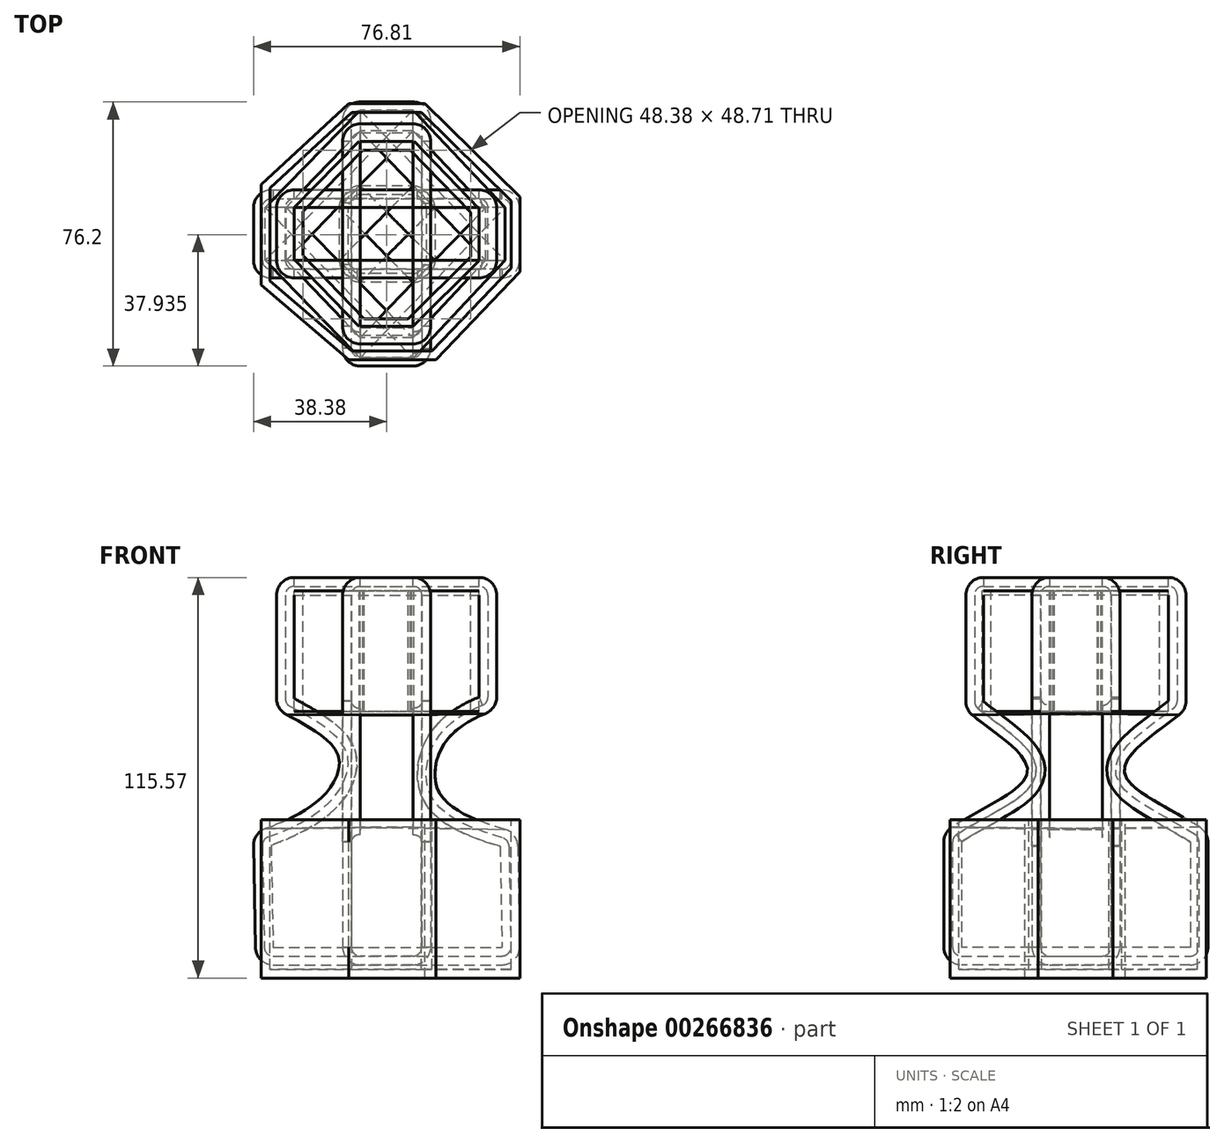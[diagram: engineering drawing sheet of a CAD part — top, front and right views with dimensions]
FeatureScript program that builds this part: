
annotation { "Feature Type Name" : "Feature", "Feature Type Description" : "" }
export const myFeature = defineFeature(function(context is Context, id is Id, definition is map)
    precondition{}
    {
        {
            var Q0;
            Q0=qCreatedBy(makeId("Front.planeOp"),FACE);
            var sketch = newSketch(context, id + "F0", { "sketchPlane" : qUnion([Q0])});
            skLineSegment(sketch, "E0.bottom", {"start": v(-38.45, 19.05) * mm, "end": v(37.75, 19.05) * mm});
            skLineSegment(sketch, "E0.top", {"start": v(-37.75, -19.05) * mm, "end": v(38.45, -19.05) * mm});
            skLineSegment(sketch, "E0.left", {"start": v(-38.45, 19.05) * mm, "end": v(-37.75, -19.05) * mm});
            skLineSegment(sketch, "E0.right", {"start": v(37.75, 19.05) * mm, "end": v(38.45, -19.05) * mm});
            skPoint(sketch, "E0.middle", {"position": v(0, 0) * mm});
            skLineSegment(sketch, "E1.bottom", {"start": v(-31.75, 92.7) * mm, "end": v(31.75, 92.7) * mm});
            skLineSegment(sketch, "E1.top", {"start": v(-31.75, 54.6) * mm, "end": v(31.75, 54.6) * mm});
            skLineSegment(sketch, "E1.left", {"start": v(-31.75, 92.7) * mm, "end": v(-31.75, 54.6) * mm});
            skLineSegment(sketch, "E1.right", {"start": v(31.75, 92.7) * mm, "end": v(31.75, 54.6) * mm});
            skPoint(sketch, "E1.middle", {"position": v(0, 73.66) * mm});
            skFitSpline(sketch, "E2", {"points": [v(31.75, 54.6) * mm, v(13.97, 36.83) * mm, v(37.75, 19.05) * mm], "startDerivative": vector(-85.25, -26.82) * mm, "endDerivative": vector(119.34, -30.7) * mm});
            skFitSpline(sketch, "E3", {"points": [v(-31.75, 54.6) * mm, v(-13.97, 36.83) * mm, v(-38.45, 19.05) * mm], "startDerivative": vector(109.16, -53.78) * mm, "endDerivative": vector(-101.51, -32.91) * mm});
            skSolve(sketch);
        }
        {
            var Q0;
            Q0=makeQuery(id+"F0.imprint","IMPRINT",FACE,{"disambiguationData":[TD([[makeQuery(id+"F0.imprint","IMPRINT",EDGE,{"derivedFrom":sQuery(id+"F0.wireOp",EDGE,"E1.bottom")}),-1.0]])]});
            var Q1;
            Q1=makeQuery(id+"F0.imprint","IMPRINT",FACE,{"disambiguationData":[TD([[makeQuery(id+"F0.imprint","IMPRINT",EDGE,{"derivedFrom":sQuery(id+"F0.wireOp",EDGE,"E0.bottom")}),-1.0]])]});
            var Q2;
            Q2=makeQuery(id+"F0.imprint","IMPRINT",FACE,{"disambiguationData":[TD([[makeQuery(id+"F0.imprint","IMPRINT",EDGE,{"derivedFrom":sQuery(id+"F0.wireOp",EDGE,"E0.bottom")}),1.0]])]});
            extrude(context, id + "F1", {"entities" : qUnion([Q0, Q1, Q2]), "endBound" : BoundingType.SYMMETRIC, "depth" : 25.4 * mm});
        }
        {
            var Q0;
            Q0=qCreatedBy(makeId("Right.planeOp"),FACE);
            var sketch = newSketch(context, id + "F2", { "sketchPlane" : qUnion([Q0])});
            skLineSegment(sketch, "E4.bottom", {"start": v(38.1, 19.05) * mm, "end": v(-38.1, 19.05) * mm});
            skLineSegment(sketch, "E4.top", {"start": v(38.1, -19.05) * mm, "end": v(-38.1, -19.05) * mm});
            skLineSegment(sketch, "E4.left", {"start": v(38.1, 19.05) * mm, "end": v(38.1, -19.05) * mm});
            skLineSegment(sketch, "E4.right", {"start": v(-38.1, 19.05) * mm, "end": v(-38.1, -19.05) * mm});
            skPoint(sketch, "E4.middle", {"position": v(0, 0) * mm});
            skLineSegment(sketch, "E5.bottom", {"start": v(31.75, 54.61) * mm, "end": v(-31.75, 54.6) * mm});
            skLineSegment(sketch, "E5.top", {"start": v(31.75, 92.7) * mm, "end": v(-31.75, 92.7) * mm});
            skLineSegment(sketch, "E5.left", {"start": v(31.75, 54.61) * mm, "end": v(31.75, 92.7) * mm});
            skLineSegment(sketch, "E5.right", {"start": v(-31.75, 54.6) * mm, "end": v(-31.75, 92.7) * mm});
            skPoint(sketch, "E5.middle", {"position": v(0, 73.66) * mm});
            skFitSpline(sketch, "E6", {"points": [v(31.75, 54.61) * mm, v(13.97, 36.83) * mm, v(38.1, 19.05) * mm], "startDerivative": vector(-45.66, -37.2) * mm, "endDerivative": vector(56.1, -40.08) * mm});
            skFitSpline(sketch, "E7", {"points": [v(-31.75, 54.6) * mm, v(-13.97, 36.83) * mm, v(-38.1, 19.05) * mm], "startDerivative": vector(37.02, -34.46) * mm, "endDerivative": vector(-47.7, -36.6) * mm});
            skSolve(sketch);
        }
        {
            var Q0;
            Q0=makeQuery(id+"F2.imprint","IMPRINT",FACE,{"disambiguationData":[TD([[makeQuery(id+"F2.imprint","IMPRINT",EDGE,{"derivedFrom":sQuery(id+"F2.wireOp",EDGE,"E5.bottom")}),-1.0]])]});
            var Q1;
            Q1=makeQuery(id+"F2.imprint","IMPRINT",FACE,{"disambiguationData":[TD([[makeQuery(id+"F2.imprint","IMPRINT",EDGE,{"derivedFrom":sQuery(id+"F2.wireOp",EDGE,"E4.bottom")}),-1.0]])]});
            var Q2;
            Q2=makeQuery(id+"F2.imprint","IMPRINT",FACE,{"disambiguationData":[TD([[makeQuery(id+"F2.imprint","IMPRINT",EDGE,{"derivedFrom":sQuery(id+"F2.wireOp",EDGE,"E4.bottom")}),1.0]])]});
            extrude(context, id + "F3", {"entities" : qUnion([Q0, Q1, Q2]), "endBound" : BoundingType.SYMMETRIC, "depth" : 25.4 * mm});
        }
        {
            var Q0;
            Q0=makeQuery(id+"F1.opExtrude","SWEPT_EDGE",EDGE,{"disambiguationData":[OSD([sQuery(id+"F0.wireOp",EDGE,"E1.bottom"),sQuery(id+"F0.wireOp",EDGE,"E1.right")])]});
            var Q1;
            Q1=makeQuery(id+"F1.opExtrude","SWEPT_EDGE",EDGE,{"disambiguationData":[OSD([sQuery(id+"F0.wireOp",EDGE,"E0.top"),sQuery(id+"F0.wireOp",EDGE,"E0.right")])]});
            var Q2;
            Q2=makeQuery(id+"F1.opExtrude","SWEPT_EDGE",EDGE,{"disambiguationData":[OSD([sQuery(id+"F0.wireOp",EDGE,"E0.top"),sQuery(id+"F0.wireOp",EDGE,"E0.left")])]});
            var Q3;
            Q3=makeQuery(id+"F1.opExtrude","CAP_EDGE",EDGE,{"disambiguationData":[OSD([sQuery(id+"F0.wireOp",EDGE,"E0.right")])],"isStart":false});
            var Q4;
            Q4=makeQuery(id+"F1.opExtrude","CAP_EDGE",EDGE,{"disambiguationData":[OSD([sQuery(id+"F0.wireOp",EDGE,"E2")])],"isStart":false});
            var Q5;
            Q5=makeQuery(id+"F1.opExtrude","CAP_EDGE",EDGE,{"disambiguationData":[OSD([sQuery(id+"F0.wireOp",EDGE,"E2")])],"isStart":true});
            var Q6;
            Q6=makeQuery(id+"F3.opExtrude","CAP_EDGE",EDGE,{"disambiguationData":[OSD([sQuery(id+"F2.wireOp",EDGE,"E7")])],"isStart":false});
            var Q7;
            Q7=makeQuery(id+"F3.opExtrude","CAP_EDGE",EDGE,{"disambiguationData":[OSD([sQuery(id+"F2.wireOp",EDGE,"E5.right")])],"isStart":false});
            var Q8;
            Q8=makeQuery(id+"F3.opExtrude","CAP_EDGE",EDGE,{"disambiguationData":[OSD([sQuery(id+"F2.wireOp",EDGE,"E6")])],"isStart":false});
            var Q9;
            Q9=makeQuery(id+"F3.opExtrude","CAP_EDGE",EDGE,{"disambiguationData":[OSD([sQuery(id+"F2.wireOp",EDGE,"E5.left")])],"isStart":true});
            var Q10;
            Q10=makeQuery(id+"F3.opExtrude","CAP_EDGE",EDGE,{"disambiguationData":[OSD([sQuery(id+"F2.wireOp",EDGE,"E5.left")])],"isStart":false});
            var Q11;
            Q11=makeQuery(id+"F3.opExtrude","CAP_EDGE",EDGE,{"disambiguationData":[OSD([sQuery(id+"F2.wireOp",EDGE,"E6")])],"isStart":true});
            var Q12;
            Q12=makeQuery(id+"F1.opExtrude","CAP_EDGE",EDGE,{"disambiguationData":[OSD([sQuery(id+"F0.wireOp",EDGE,"E0.right")])],"isStart":true});
            var Q13;
            Q13=makeQuery(id+"F1.opExtrude","CAP_EDGE",EDGE,{"disambiguationData":[OSD([sQuery(id+"F0.wireOp",EDGE,"E0.left")])],"isStart":false});
            var Q14;
            Q14=makeQuery(id+"F1.opExtrude","CAP_EDGE",EDGE,{"disambiguationData":[OSD([sQuery(id+"F0.wireOp",EDGE,"E0.top")])],"isStart":false});
            var Q15;
            Q15=makeQuery(id+"F1.opExtrude","CAP_EDGE",EDGE,{"disambiguationData":[OSD([sQuery(id+"F0.wireOp",EDGE,"E0.top")])],"isStart":true});
            var Q16;
            Q16=makeQuery(id+"F1.opExtrude","SWEPT_EDGE",EDGE,{"disambiguationData":[OSD([sQuery(id+"F0.wireOp",EDGE,"E1.top"),sQuery(id+"F0.wireOp",EDGE,"E1.right"),sQuery(id+"F0.wireOp",EDGE,"E2")])]});
            var Q17;
            Q17=makeQuery(id+"F1.opExtrude","SWEPT_EDGE",EDGE,{"disambiguationData":[OSD([sQuery(id+"F0.wireOp",EDGE,"E1.bottom"),sQuery(id+"F0.wireOp",EDGE,"E1.left")])]});
            var Q18;
            Q18=makeQuery(id+"F1.opExtrude","SWEPT_EDGE",EDGE,{"disambiguationData":[OSD([sQuery(id+"F0.wireOp",EDGE,"E0.bottom"),sQuery(id+"F0.wireOp",EDGE,"E0.right"),sQuery(id+"F0.wireOp",EDGE,"E2")])]});
            var Q19;
            Q19=makeQuery(id+"F1.opExtrude","CAP_EDGE",EDGE,{"disambiguationData":[OSD([sQuery(id+"F0.wireOp",EDGE,"E1.bottom")])],"isStart":false});
            var Q20;
            Q20=makeQuery(id+"F1.opExtrude","CAP_EDGE",EDGE,{"disambiguationData":[OSD([sQuery(id+"F0.wireOp",EDGE,"E1.bottom")])],"isStart":true});
            var Q21;
            Q21=makeQuery(id+"F1.opExtrude","CAP_EDGE",EDGE,{"disambiguationData":[OSD([sQuery(id+"F0.wireOp",EDGE,"E3")])],"isStart":false});
            var Q22;
            Q22=makeQuery(id+"F1.opExtrude","CAP_EDGE",EDGE,{"disambiguationData":[OSD([sQuery(id+"F0.wireOp",EDGE,"E3")])],"isStart":true});
            var Q23;
            Q23=makeQuery(id+"F1.opExtrude","CAP_EDGE",EDGE,{"disambiguationData":[OSD([sQuery(id+"F0.wireOp",EDGE,"E1.right")])],"isStart":false});
            var Q24;
            Q24=makeQuery(id+"F1.opExtrude","CAP_EDGE",EDGE,{"disambiguationData":[OSD([sQuery(id+"F0.wireOp",EDGE,"E1.right")])],"isStart":true});
            var Q25;
            Q25=makeQuery(id+"F3.opExtrude","CAP_EDGE",EDGE,{"disambiguationData":[OSD([sQuery(id+"F2.wireOp",EDGE,"E4.left")])],"isStart":true});
            var Q26;
            Q26=makeQuery(id+"F3.opExtrude","CAP_EDGE",EDGE,{"disambiguationData":[OSD([sQuery(id+"F2.wireOp",EDGE,"E4.left")])],"isStart":false});
            var Q27;
            Q27=makeQuery(id+"F3.opExtrude","CAP_EDGE",EDGE,{"disambiguationData":[OSD([sQuery(id+"F2.wireOp",EDGE,"E7")])],"isStart":true});
            var Q28;
            Q28=makeQuery(id+"F3.opExtrude","CAP_EDGE",EDGE,{"disambiguationData":[OSD([sQuery(id+"F2.wireOp",EDGE,"E5.top")])],"isStart":false});
            var Q29;
            Q29=makeQuery(id+"F3.opExtrude","SWEPT_EDGE",EDGE,{"disambiguationData":[OSD([sQuery(id+"F2.wireOp",EDGE,"E4.top"),sQuery(id+"F2.wireOp",EDGE,"E4.left")])]});
            var Q30;
            Q30=makeQuery(id+"F3.opExtrude","CAP_EDGE",EDGE,{"disambiguationData":[OSD([sQuery(id+"F2.wireOp",EDGE,"E4.right")])],"isStart":false});
            var Q31;
            Q31=makeQuery(id+"F3.opExtrude","SWEPT_EDGE",EDGE,{"disambiguationData":[OSD([sQuery(id+"F2.wireOp",EDGE,"E5.bottom"),sQuery(id+"F2.wireOp",EDGE,"E5.left"),sQuery(id+"F2.wireOp",EDGE,"E6")])]});
            var Q32;
            Q32=makeQuery(id+"F3.opExtrude","CAP_EDGE",EDGE,{"disambiguationData":[OSD([sQuery(id+"F2.wireOp",EDGE,"E4.top")])],"isStart":true});
            var Q33;
            Q33=makeQuery(id+"F3.opExtrude","CAP_EDGE",EDGE,{"disambiguationData":[OSD([sQuery(id+"F2.wireOp",EDGE,"E4.right")])],"isStart":true});
            var Q34;
            Q34=makeQuery(id+"F3.opExtrude","SWEPT_EDGE",EDGE,{"disambiguationData":[OSD([sQuery(id+"F2.wireOp",EDGE,"E4.bottom"),sQuery(id+"F2.wireOp",EDGE,"E4.left"),sQuery(id+"F2.wireOp",EDGE,"E6")])]});
            var Q35;
            Q35=makeQuery(id+"F3.opExtrude","CAP_EDGE",EDGE,{"disambiguationData":[OSD([sQuery(id+"F2.wireOp",EDGE,"E4.top")])],"isStart":false});
            var Q36;
            Q36=makeQuery(id+"F3.opExtrude","CAP_EDGE",EDGE,{"disambiguationData":[OSD([sQuery(id+"F2.wireOp",EDGE,"E5.top")])],"isStart":true});
            var Q37;
            Q37=makeQuery(id+"F3.opExtrude","SWEPT_EDGE",EDGE,{"disambiguationData":[OSD([sQuery(id+"F2.wireOp",EDGE,"E5.bottom"),sQuery(id+"F2.wireOp",EDGE,"E5.right"),sQuery(id+"F2.wireOp",EDGE,"E7")])]});
            var Q38;
            Q38=makeQuery(id+"F1.opExtrude","CAP_EDGE",EDGE,{"disambiguationData":[OSD([sQuery(id+"F0.wireOp",EDGE,"E1.left")])],"isStart":false});
            var Q39;
            Q39=makeQuery(id+"F1.opExtrude","CAP_EDGE",EDGE,{"disambiguationData":[OSD([sQuery(id+"F0.wireOp",EDGE,"E1.left")])],"isStart":true});
            var Q40;
            Q40=makeQuery(id+"F1.opExtrude","CAP_EDGE",EDGE,{"disambiguationData":[OSD([sQuery(id+"F0.wireOp",EDGE,"E0.left")])],"isStart":true});
            var Q41;
            Q41=makeQuery(id+"F1.opExtrude","SWEPT_EDGE",EDGE,{"disambiguationData":[OSD([sQuery(id+"F0.wireOp",EDGE,"E1.top"),sQuery(id+"F0.wireOp",EDGE,"E1.left"),sQuery(id+"F0.wireOp",EDGE,"E3")])]});
            var Q42;
            Q42=makeQuery(id+"F1.opExtrude","SWEPT_EDGE",EDGE,{"disambiguationData":[OSD([sQuery(id+"F0.wireOp",EDGE,"E0.bottom"),sQuery(id+"F0.wireOp",EDGE,"E0.left"),sQuery(id+"F0.wireOp",EDGE,"E3")])]});
            var Q43;
            Q43=makeQuery(id+"F3.opExtrude","SWEPT_EDGE",EDGE,{"disambiguationData":[OSD([sQuery(id+"F2.wireOp",EDGE,"E4.bottom"),sQuery(id+"F2.wireOp",EDGE,"E4.right"),sQuery(id+"F2.wireOp",EDGE,"E7")])]});
            var Q44;
            Q44=makeQuery(id+"F3.opExtrude","SWEPT_EDGE",EDGE,{"disambiguationData":[OSD([sQuery(id+"F2.wireOp",EDGE,"E5.top"),sQuery(id+"F2.wireOp",EDGE,"E5.right")])]});
            var Q45;
            Q45=makeQuery(id+"F3.opExtrude","SWEPT_EDGE",EDGE,{"disambiguationData":[OSD([sQuery(id+"F2.wireOp",EDGE,"E5.top"),sQuery(id+"F2.wireOp",EDGE,"E5.left")])]});
            var Q46;
            Q46=makeQuery(id+"F3.opExtrude","CAP_EDGE",EDGE,{"disambiguationData":[OSD([sQuery(id+"F2.wireOp",EDGE,"E5.right")])],"isStart":true});
            var Q47;
            Q47=makeQuery(id+"F3.opExtrude","SWEPT_EDGE",EDGE,{"disambiguationData":[OSD([sQuery(id+"F2.wireOp",EDGE,"E4.top"),sQuery(id+"F2.wireOp",EDGE,"E4.right")])]});
            fillet(context, id + "F4", {"entities" : qUnion([Q0, Q1, Q2, Q3, Q4, Q5, Q6, Q7, Q8, Q9, Q10, Q11, Q12, Q13, Q14, Q15, Q16, Q17, Q18, Q19, Q20, Q21, Q22, Q23, Q24, Q25, Q26, Q27, Q28, Q29, Q30, Q31, Q32, Q33, Q34, Q35, Q36, Q37, Q38, Q39, Q40, Q41, Q42, Q43, Q44, Q45, Q46, Q47]), "radius" : 5.08 * mm, "tangentPropagation" : true, "allowEdgeOverflow" : false});
        }
        {
            var Q0;
            Q0=makeQuery(id+"F1.opExtrude","SWEPT_FACE",FACE,{"disambiguationData":[OSD([sQuery(id+"F0.wireOp",EDGE,"E1.bottom")])]});
            var Q1;
            Q1=makeQuery(id+"F3.opExtrude","SWEPT_FACE",FACE,{"disambiguationData":[OSD([sQuery(id+"F2.wireOp",EDGE,"E5.top")])]});
            var Q2;
            Q2=makeQuery(id+"F3.opExtrude","CAP_FACE",FACE,{"disambiguationData":[OSD([sQuery(id+"F2.wireOp",EDGE,"E4.top"),sQuery(id+"F2.wireOp",EDGE,"E4.left"),sQuery(id+"F2.wireOp",EDGE,"E4.right"),sQuery(id+"F2.wireOp",EDGE,"E5.top"),sQuery(id+"F2.wireOp",EDGE,"E5.left"),sQuery(id+"F2.wireOp",EDGE,"E5.right"),sQuery(id+"F2.wireOp",EDGE,"E6"),sQuery(id+"F2.wireOp",EDGE,"E7")])],"isStart":true});
            var Q3;
            Q3=makeQuery(id+"F1.opExtrude","CAP_FACE",FACE,{"disambiguationData":[OSD([sQuery(id+"F0.wireOp",EDGE,"E0.top"),sQuery(id+"F0.wireOp",EDGE,"E0.left"),sQuery(id+"F0.wireOp",EDGE,"E0.right"),sQuery(id+"F0.wireOp",EDGE,"E1.bottom"),sQuery(id+"F0.wireOp",EDGE,"E1.left"),sQuery(id+"F0.wireOp",EDGE,"E1.right"),sQuery(id+"F0.wireOp",EDGE,"E2"),sQuery(id+"F0.wireOp",EDGE,"E3")])],"isStart":true});
            var Q4;
            Q4=makeQuery(id+"F3.opExtrude","CAP_FACE",FACE,{"disambiguationData":[OSD([sQuery(id+"F2.wireOp",EDGE,"E4.top"),sQuery(id+"F2.wireOp",EDGE,"E4.left"),sQuery(id+"F2.wireOp",EDGE,"E4.right"),sQuery(id+"F2.wireOp",EDGE,"E5.top"),sQuery(id+"F2.wireOp",EDGE,"E5.left"),sQuery(id+"F2.wireOp",EDGE,"E5.right"),sQuery(id+"F2.wireOp",EDGE,"E6"),sQuery(id+"F2.wireOp",EDGE,"E7")])],"isStart":false});
            var Q5;
            Q5=makeQuery(id+"F1.opExtrude","CAP_FACE",FACE,{"disambiguationData":[OSD([sQuery(id+"F0.wireOp",EDGE,"E0.top"),sQuery(id+"F0.wireOp",EDGE,"E0.left"),sQuery(id+"F0.wireOp",EDGE,"E0.right"),sQuery(id+"F0.wireOp",EDGE,"E1.bottom"),sQuery(id+"F0.wireOp",EDGE,"E1.left"),sQuery(id+"F0.wireOp",EDGE,"E1.right"),sQuery(id+"F0.wireOp",EDGE,"E2"),sQuery(id+"F0.wireOp",EDGE,"E3")])],"isStart":false});
            shell(context, id + "F5", {"entities" : qUnion([Q0, Q1, Q2, Q3, Q4, Q5]), "thickness" : 2.54 * mm});
        }
        {
            var Q0;
            Q0=qCreatedBy(makeId("Top.planeOp"),FACE);
            var sketch = newSketch(context, id + "F6", { "sketchPlane" : qUnion([Q0])});
            skLineSegment(sketch, "E8", {"start": v(-11.25, 34.28) * mm, "end": v(-10.99, 34.28) * mm});
            skLineSegment(sketch, "E9", {"start": v(-36.23, 14.3) * mm, "end": v(-10.99, 37.64) * mm});
            skLineSegment(sketch, "E10", {"start": v(-10.99, 37.64) * mm, "end": v(11.02, 37.64) * mm});
            skLineSegment(sketch, "E11", {"start": v(11.02, 37.64) * mm, "end": v(38.43, 10.67) * mm});
            skLineSegment(sketch, "E12", {"start": v(38.43, 10.67) * mm, "end": v(38.43, -10.95) * mm});
            skLineSegment(sketch, "E13", {"start": v(38.43, -10.95) * mm, "end": v(14.16, -36.26) * mm});
            skLineSegment(sketch, "E14", {"start": v(14.16, -36.26) * mm, "end": v(-10.95, -36.26) * mm});
            skLineSegment(sketch, "E15", {"start": v(-10.95, -36.26) * mm, "end": v(-36.23, -14.73) * mm});
            skLineSegment(sketch, "E16", {"start": v(-36.23, -14.73) * mm, "end": v(-36.23, 14.3) * mm});
            skSolve(sketch);
        }
        {
            var Q0;
            Q0 = qSketchRegion(id + "F6", true);
            extrude(context, id + "F7", {"entities" : qUnion([Q0]), "endBound" : BoundingType.SYMMETRIC, "oppositeDirection" : true, "depth" : 45.72 * mm});
        }
        {
            var Q0;
            Q0=makeQuery(id+"F7.opExtrude","CAP_FACE",FACE,{"disambiguationData":[OSD([sQuery(id+"F6.wireOp",EDGE,"E9"),sQuery(id+"F6.wireOp",EDGE,"E10"),sQuery(id+"F6.wireOp",EDGE,"E11"),sQuery(id+"F6.wireOp",EDGE,"E12"),sQuery(id+"F6.wireOp",EDGE,"E13"),sQuery(id+"F6.wireOp",EDGE,"E14"),sQuery(id+"F6.wireOp",EDGE,"E15"),sQuery(id+"F6.wireOp",EDGE,"E16")])],"isStart":true});
            shell(context, id + "F8", {"entities" : qUnion([Q0]), "thickness" : 2.54 * mm});
        }
        {
            var Q0;
            Q0=qCreatedBy(makeId("Top.planeOp"),FACE);
            cPlane(context, id + "F9", {"entities" : qUnion([Q0]), "cplaneType" : CPlaneType.OFFSET, "offset" : 88.9 * mm, "width" : 152.4 * mm, "height" : 152.4 * mm});
        }
        {
            var Q0;
            Q0=qCreatedBy(id+"F9.planeOp",FACE);
            var sketch = newSketch(context, id + "F10", { "sketchPlane" : qUnion([Q0])});
            skLineSegment(sketch, "E17", {"start": v(-7.6, -27.06) * mm, "end": v(7.26, -27.06) * mm});
            skLineSegment(sketch, "E18", {"start": v(7.26, -27.06) * mm, "end": v(26.73, -7.6) * mm});
            skLineSegment(sketch, "E19", {"start": v(26.73, -7.6) * mm, "end": v(26.73, 7.26) * mm});
            skLineSegment(sketch, "E20", {"start": v(26.73, 7.26) * mm, "end": v(7.92, 26.73) * mm});
            skLineSegment(sketch, "E21", {"start": v(7.92, 26.73) * mm, "end": v(-7.92, 26.73) * mm});
            skLineSegment(sketch, "E22", {"start": v(-7.92, 26.73) * mm, "end": v(-26.73, 7.6) * mm});
            skLineSegment(sketch, "E23", {"start": v(-26.73, 7.6) * mm, "end": v(-26.73, -7.26) * mm});
            skLineSegment(sketch, "E24", {"start": v(-26.73, -7.26) * mm, "end": v(-7.6, -27.06) * mm});
            skSolve(sketch);
        }
        {
            var Q0;
            Q0=makeQuery(id+"F10.imprint","IMPRINT",FACE,{"disambiguationData":[TD([[makeQuery(id+"F10.imprint","IMPRINT",EDGE,{"derivedFrom":sQuery(id+"F10.wireOp",EDGE,"E17")}),1.0]])]});
            extrude(context, id + "F11", {"entities" : qUnion([Q0]), "oppositeDirection" : true, "depth" : 34.8 * mm});
        }
        {
            var Q0;
            Q0=makeQuery(id+"F11.opExtrude","CAP_FACE",FACE,{"disambiguationData":[OSD([sQuery(id+"F10.wireOp",EDGE,"E17"),sQuery(id+"F10.wireOp",EDGE,"E18"),sQuery(id+"F10.wireOp",EDGE,"E19"),sQuery(id+"F10.wireOp",EDGE,"E20"),sQuery(id+"F10.wireOp",EDGE,"E21"),sQuery(id+"F10.wireOp",EDGE,"E22"),sQuery(id+"F10.wireOp",EDGE,"E23"),sQuery(id+"F10.wireOp",EDGE,"E24")])],"isStart":false});
            var Q1;
            Q1=makeQuery(id+"F11.opExtrude","CAP_FACE",FACE,{"disambiguationData":[OSD([sQuery(id+"F10.wireOp",EDGE,"E17"),sQuery(id+"F10.wireOp",EDGE,"E18"),sQuery(id+"F10.wireOp",EDGE,"E19"),sQuery(id+"F10.wireOp",EDGE,"E20"),sQuery(id+"F10.wireOp",EDGE,"E21"),sQuery(id+"F10.wireOp",EDGE,"E22"),sQuery(id+"F10.wireOp",EDGE,"E23"),sQuery(id+"F10.wireOp",EDGE,"E24")])],"isStart":true});
            shell(context, id + "F12", {"entities" : qUnion([Q0, Q1]), "thickness" : 2.54 * mm});
        }
        {
            var Q0;
            Q0=makeQuery(id+"F3.opExtrude","SWEPT_FACE",FACE,{"disambiguationData":[OSD([sQuery(id+"F2.wireOp",EDGE,"E7")])]});
            var Q1;
            Q1=makeQuery(id+"F1.opExtrude","SWEPT_FACE",FACE,{"disambiguationData":[OSD([sQuery(id+"F0.wireOp",EDGE,"E2")])]});
            loft(context, id + "F13", {"sheetProfilesArray" : [{ "sheetProfileEntities" : qUnion([Q0]) }, { "sheetProfileEntities" : qUnion([Q1]) }]});
        }
        {
            var Q0;
            Q0=makeQuery(id+"F3.opExtrude","SWEPT_FACE",FACE,{"disambiguationData":[OSD([sQuery(id+"F2.wireOp",EDGE,"E6")])]});
            var Q1;
            Q1=makeQuery(id+"F1.opExtrude","SWEPT_FACE",FACE,{"disambiguationData":[OSD([sQuery(id+"F0.wireOp",EDGE,"E2")])]});
            loft(context, id + "F14", {"sheetProfilesArray" : [{ "sheetProfileEntities" : qUnion([Q0]) }, { "sheetProfileEntities" : qUnion([Q1]) }]});
        }
        {
            var Q0;
            Q0=makeQuery(id+"F3.opExtrude","SWEPT_FACE",FACE,{"disambiguationData":[OSD([sQuery(id+"F2.wireOp",EDGE,"E6")])]});
            var Q1;
            Q1=makeQuery(id+"F1.opExtrude","SWEPT_FACE",FACE,{"disambiguationData":[OSD([sQuery(id+"F0.wireOp",EDGE,"E3")])]});
            loft(context, id + "F15", {"sheetProfilesArray" : [{ "sheetProfileEntities" : qUnion([Q0]) }, { "sheetProfileEntities" : qUnion([Q1]) }]});
        }
        {
            var Q0;
            Q0=makeQuery(id+"F15.opLoft","CAP_FACE",FACE,{"disambiguationData":[OSD([sQuery(id+"F0.wireOp",EDGE,"E3")])],"isStart":true});
            var Q1;
            Q1=makeQuery(id+"F3.opExtrude","SWEPT_FACE",FACE,{"disambiguationData":[OSD([sQuery(id+"F2.wireOp",EDGE,"E7")])]});
            loft(context, id + "F16", {"sheetProfilesArray" : [{ "sheetProfileEntities" : qUnion([Q0]) }, { "sheetProfileEntities" : qUnion([Q1]) }]});
        }
    });
